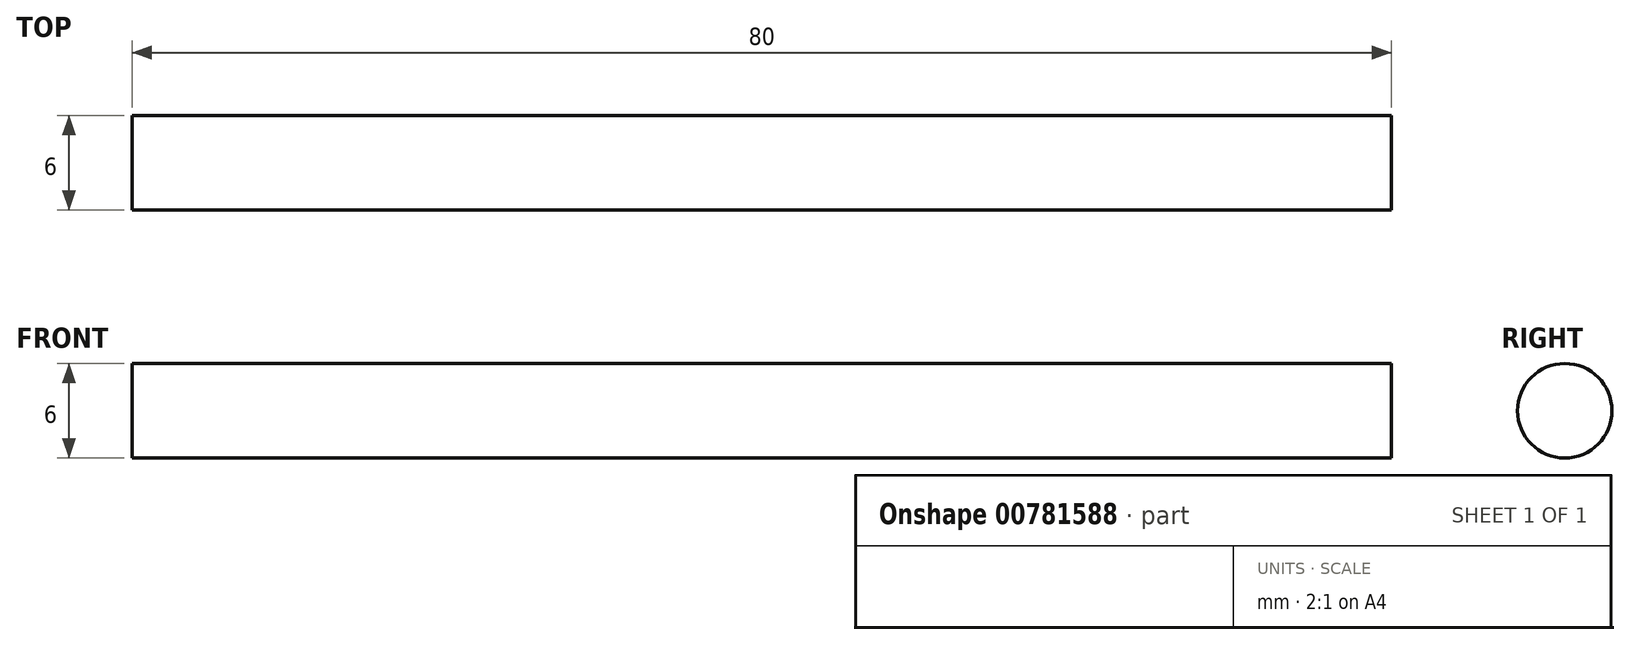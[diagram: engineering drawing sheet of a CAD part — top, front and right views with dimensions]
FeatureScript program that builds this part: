
annotation { "Feature Type Name" : "Feature", "Feature Type Description" : "" }
export const myFeature = defineFeature(function(context is Context, id is Id, definition is map)
    precondition{}
    {
        {
            var Q0;
            Q0=qCreatedBy(makeId("Right.planeOp"),FACE);
            var sketch = newSketch(context, id + "F0", { "sketchPlane" : qUnion([Q0])});
            skCircle(sketch, "E0", {"center": v(0, 0) * mm, "radius": 3 * mm});
            skSolve(sketch);
        }
        {
            var Q0;
            Q0 = qSketchRegion(id + "F0", true);
            extrude(context, id + "F1", {"entities" : qUnion([Q0]), "endBound" : BoundingType.SYMMETRIC, "depth" : 80 * mm, "offsetDistance" : 25 * mm});
        }
    });
